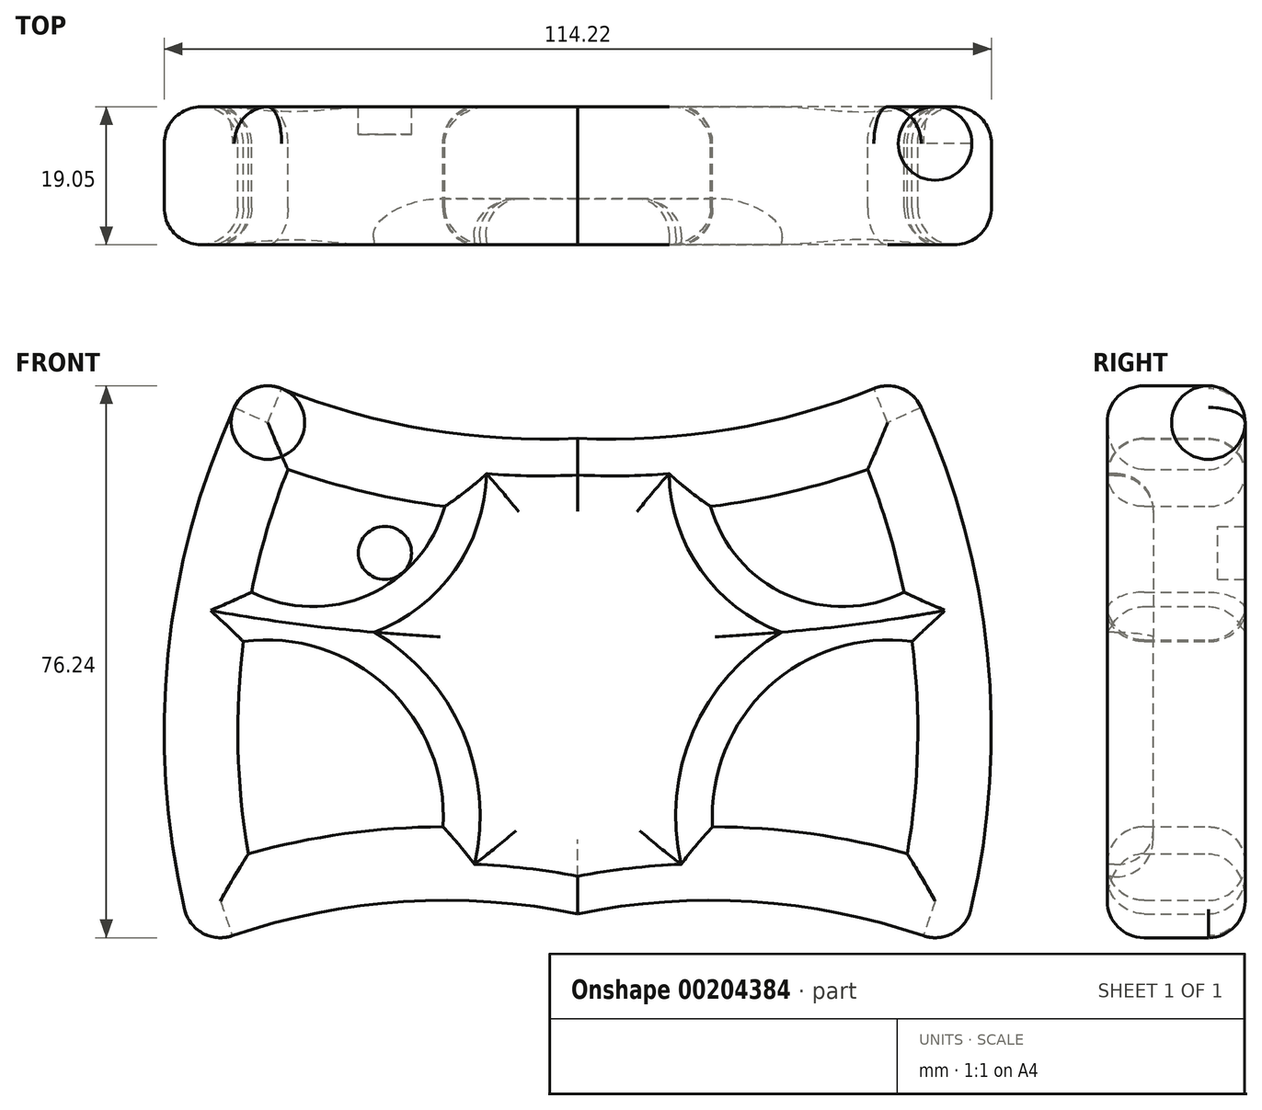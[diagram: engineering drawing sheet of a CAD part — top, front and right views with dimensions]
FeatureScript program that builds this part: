
annotation { "Feature Type Name" : "Feature", "Feature Type Description" : "" }
export const myFeature = defineFeature(function(context is Context, id is Id, definition is map)
    precondition{}
    {
        {
            var Q0;
            Q0=qCreatedBy(makeId("Front.planeOp"),FACE);
            var sketch = newSketch(context, id + "F0", { "sketchPlane" : qUnion([Q0])});
            skArc(sketch, "E0", {"start": v(0, 27) * mm, "mid": v(23.16, 28.63) * mm, "end": v(45.25, 35.77) * mm});
            skArc(sketch, "E1", {"start": v(52.85, -43.65) * mm, "mid": v(56.62, -3.22) * mm, "end": v(45.25, 35.77) * mm});
            skArc(sketch, "E2", {"start": v(52.85, -43.65) * mm, "mid": v(26.8, -37.23) * mm, "end": v(0, -38.69) * mm});
            skArc(sketch, "E3.0", {"start": v(43.09, -40.83) * mm, "mid": v(43.16, -40.57) * mm, "end": v(43.23, -40.32) * mm});
            skArc(sketch, "E4.0", {"start": v(0, 16.83) * mm, "mid": v(20.3, 17.85) * mm, "end": v(40.03, 22.7) * mm});
            skArc(sketch, "E5.0", {"start": v(56.7, -34.25) * mm, "mid": v(55.97, -33.95) * mm, "end": v(55.23, -33.66) * mm});
            skArc(sketch, "E6.trimOffspring", {"start": v(49.45, 26.51) * mm, "mid": v(49.48, 26.53) * mm, "end": v(49.52, 26.54) * mm});
            skArc(sketch, "E7.trimOffspring", {"start": v(45.5, -30.4) * mm, "mid": v(22.87, -26.77) * mm, "end": v(0, -28.34) * mm});
            skArc(sketch, "E8.trimOffspring", {"start": v(45.5, -30.4) * mm, "mid": v(46.44, -3.47) * mm, "end": v(40.03, 22.7) * mm});
            skPoint(sketch, "E9", {"position": v(0, -28.34) * mm});
            skPoint(sketch, "E10", {"position": v(0, 16.83) * mm});
            skArc(sketch, "E11", {"start": v(18.36, 17.58) * mm, "mid": v(28.9, 5.37) * mm, "end": v(45.04, 5.76) * mm});
            skArc(sketch, "E12", {"start": v(46.16, -1.09) * mm, "mid": v(26.35, -7.37) * mm, "end": v(18.62, -26.67) * mm});
            skPoint(sketch, "E13", {"position": v(23.95, 8.57) * mm});
            skPoint(sketch, "E14", {"position": v(28.28, 5.66) * mm});
            skArc(sketch, "E15.MirrorCS", {"start": v(0, 27) * mm, "mid": v(-23.16, 28.63) * mm, "end": v(-45.25, 35.77) * mm});
            skArc(sketch, "E16.MirrorCS", {"start": v(-52.85, -43.65) * mm, "mid": v(-56.62, -3.22) * mm, "end": v(-45.25, 35.77) * mm});
            skArc(sketch, "E17.MirrorCS", {"start": v(-49.45, 26.51) * mm, "mid": v(-49.48, 26.53) * mm, "end": v(-49.52, 26.54) * mm});
            skArc(sketch, "E18.MirrorCS", {"start": v(-56.7, -34.25) * mm, "mid": v(-55.97, -33.95) * mm, "end": v(-55.23, -33.66) * mm});
            skArc(sketch, "E19.MirrorCS", {"start": v(-43.09, -40.83) * mm, "mid": v(-43.16, -40.57) * mm, "end": v(-43.23, -40.32) * mm});
            skPoint(sketch, "E20.MirrorP", {"position": v(-28.28, 5.66) * mm});
            skArc(sketch, "E21.MirrorCS", {"start": v(-52.85, -43.65) * mm, "mid": v(-26.8, -37.23) * mm, "end": v(0, -38.69) * mm});
            skPoint(sketch, "E22.MirrorP", {"position": v(-23.95, 8.57) * mm});
            skArc(sketch, "E23.MirrorCS", {"start": v(-46.16, -1.09) * mm, "mid": v(-26.35, -7.37) * mm, "end": v(-18.62, -26.67) * mm});
            skArc(sketch, "E24.MirrorCS", {"start": v(-18.36, 17.58) * mm, "mid": v(-28.9, 5.37) * mm, "end": v(-45.04, 5.76) * mm});
            skArc(sketch, "E25.MirrorCS", {"start": v(-45.5, -30.4) * mm, "mid": v(-22.87, -26.77) * mm, "end": v(0, -28.34) * mm});
            skArc(sketch, "E26.MirrorCS", {"start": v(-45.5, -30.4) * mm, "mid": v(-46.44, -3.47) * mm, "end": v(-40.03, 22.7) * mm});
            skArc(sketch, "E27.MirrorCS", {"start": v(0, 16.83) * mm, "mid": v(-20.3, 17.85) * mm, "end": v(-40.03, 22.7) * mm});
            skCircle(sketch, "E28", {"center": v(-27.34, 9.91) * mm, "radius": 3.18 * mm});
            skLineSegment(sketch, "E29", {"start": v(-30.28, 8.71) * mm, "end": v(-28.9, 5.37) * mm});
            skLineSegment(sketch, "E30", {"start": v(-25.02, 12.08) * mm, "end": v(-22.8, 9.7) * mm});
            skSolve(sketch);
        }
        {
            var Q0;
            Q0 = qSketchRegion(id + "F0", true);
            var Q1;
            {var subQ0=sQuery(id+"F0.wireOp",EDGE,"E11");Q1=makeQuery(id+"F0.imprint","IMPRINT",FACE,{"disambiguationData":[TD([[makeQuery(id+"F0.imprint","IMPRINT",EDGE,{"derivedFrom":subQ0}),-1.0]])]});}
            extrude(context, id + "F1", {"entities" : qUnion([Q0, Q1]), "depth" : 19.05 * mm});
        }
        {
            var Q0;
            Q0=makeQuery(id+"F1.opExtrude","CAP_EDGE",EDGE,{"disambiguationData":[OSD([sQuery(id+"F0.wireOp",EDGE,"E16.MirrorCS")])],"isStart":false});
            fillet(context, id + "F2", {"entities" : qUnion([Q0]), "radius" : 5.08 * mm, "tangentPropagation" : true, "allowEdgeOverflow" : false});
        }
        {
            var Q0;
            Q0=makeQuery(id+"F1.opExtrude","CAP_FACE",FACE,{"disambiguationData":[OSD([sQuery(id+"F0.wireOp",EDGE,"E0"),sQuery(id+"F0.wireOp",EDGE,"E1"),sQuery(id+"F0.wireOp",EDGE,"E2"),sQuery(id+"F0.wireOp",EDGE,"E4.0"),sQuery(id+"F0.wireOp",EDGE,"E7.trimOffspring"),sQuery(id+"F0.wireOp",EDGE,"E8.trimOffspring"),sQuery(id+"F0.wireOp",EDGE,"E11"),sQuery(id+"F0.wireOp",EDGE,"E12"),sQuery(id+"F0.wireOp",EDGE,"E15.MirrorCS"),sQuery(id+"F0.wireOp",EDGE,"E16.MirrorCS"),sQuery(id+"F0.wireOp",EDGE,"E21.MirrorCS"),sQuery(id+"F0.wireOp",EDGE,"E23.MirrorCS"),sQuery(id+"F0.wireOp",EDGE,"E24.MirrorCS"),sQuery(id+"F0.wireOp",EDGE,"E25.MirrorCS"),sQuery(id+"F0.wireOp",EDGE,"E26.MirrorCS"),sQuery(id+"F0.wireOp",EDGE,"E27.MirrorCS")])],"isStart":true});
            fillet(context, id + "F3", {"entities" : qUnion([Q0]), "radius" : 5.08 * mm, "tangentPropagation" : true, "allowEdgeOverflow" : false});
        }
        {
            var Q0;
            Q0=makeQuery(id+"F1.opExtrude","CAP_EDGE",EDGE,{"disambiguationData":[OSD([sQuery(id+"F0.wireOp",EDGE,"E1")])],"isStart":false});
            fillet(context, id + "F4", {"entities" : qUnion([Q0]), "radius" : 5.08 * mm, "tangentPropagation" : true, "allowEdgeOverflow" : false});
        }
        {
            var Q0;
            Q0=makeQuery(id+"F1.opExtrude","CAP_FACE",FACE,{"disambiguationData":[OSD([sQuery(id+"F0.wireOp",EDGE,"E0"),sQuery(id+"F0.wireOp",EDGE,"E1"),sQuery(id+"F0.wireOp",EDGE,"E2"),sQuery(id+"F0.wireOp",EDGE,"E4.0"),sQuery(id+"F0.wireOp",EDGE,"E7.trimOffspring"),sQuery(id+"F0.wireOp",EDGE,"E8.trimOffspring"),sQuery(id+"F0.wireOp",EDGE,"E11"),sQuery(id+"F0.wireOp",EDGE,"E12"),sQuery(id+"F0.wireOp",EDGE,"E15.MirrorCS"),sQuery(id+"F0.wireOp",EDGE,"E16.MirrorCS"),sQuery(id+"F0.wireOp",EDGE,"E21.MirrorCS"),sQuery(id+"F0.wireOp",EDGE,"E23.MirrorCS"),sQuery(id+"F0.wireOp",EDGE,"E24.MirrorCS"),sQuery(id+"F0.wireOp",EDGE,"E25.MirrorCS"),sQuery(id+"F0.wireOp",EDGE,"E26.MirrorCS"),sQuery(id+"F0.wireOp",EDGE,"E27.MirrorCS")])],"isStart":false});
            fillet(context, id + "F5", {"entities" : qUnion([Q0]), "radius" : 5.08 * mm, "tangentPropagation" : true, "allowEdgeOverflow" : false});
        }
        {
            var Q0;
            Q0=makeQuery(id+"F5.opFillet","SPLIT",FACE,{"disambiguationData":[OD(2.0)],"derivedFrom":makeQuery(id+"F1.opExtrude","CAP_FACE",FACE,{"disambiguationData":[OSD([sQuery(id+"F0.wireOp",EDGE,"E0"),sQuery(id+"F0.wireOp",EDGE,"E1"),sQuery(id+"F0.wireOp",EDGE,"E2"),sQuery(id+"F0.wireOp",EDGE,"E4.0"),sQuery(id+"F0.wireOp",EDGE,"E7.trimOffspring"),sQuery(id+"F0.wireOp",EDGE,"E8.trimOffspring"),sQuery(id+"F0.wireOp",EDGE,"E11"),sQuery(id+"F0.wireOp",EDGE,"E12"),sQuery(id+"F0.wireOp",EDGE,"E15.MirrorCS"),sQuery(id+"F0.wireOp",EDGE,"E16.MirrorCS"),sQuery(id+"F0.wireOp",EDGE,"E21.MirrorCS"),sQuery(id+"F0.wireOp",EDGE,"E23.MirrorCS"),sQuery(id+"F0.wireOp",EDGE,"E24.MirrorCS"),sQuery(id+"F0.wireOp",EDGE,"E25.MirrorCS"),sQuery(id+"F0.wireOp",EDGE,"E26.MirrorCS"),sQuery(id+"F0.wireOp",EDGE,"E27.MirrorCS")])],"isStart":false})});
            extrude(context, id + "F6", {"entities" : qUnion([Q0]), "operationType" : NewBodyOperationType.REMOVE, "oppositeDirection" : true, "depth" : 6.35 * mm, "hasDraft" : true, "draftAngle" : 3 * degree});
        }
        {
            var Q0;
            Q0=makeQuery(id+"F6.boolean.opBoolean","COPY",FACE,{"derivedFrom":makeQuery(id+"F6.opExtrude","CAP_FACE",FACE,{"disambiguationData":[OSD([sQuery(id+"F0.wireOp",EDGE,"E0"),sQuery(id+"F0.wireOp",EDGE,"E1"),sQuery(id+"F0.wireOp",EDGE,"E2"),sQuery(id+"F0.wireOp",EDGE,"E4.0"),sQuery(id+"F0.wireOp",EDGE,"E7.trimOffspring"),sQuery(id+"F0.wireOp",EDGE,"E8.trimOffspring"),sQuery(id+"F0.wireOp",EDGE,"E11"),sQuery(id+"F0.wireOp",EDGE,"E12"),sQuery(id+"F0.wireOp",EDGE,"E15.MirrorCS"),sQuery(id+"F0.wireOp",EDGE,"E16.MirrorCS"),sQuery(id+"F0.wireOp",EDGE,"E21.MirrorCS"),sQuery(id+"F0.wireOp",EDGE,"E23.MirrorCS"),sQuery(id+"F0.wireOp",EDGE,"E24.MirrorCS"),sQuery(id+"F0.wireOp",EDGE,"E25.MirrorCS"),sQuery(id+"F0.wireOp",EDGE,"E26.MirrorCS"),sQuery(id+"F0.wireOp",EDGE,"E27.MirrorCS")])],"isStart":false})});
            fillet(context, id + "F7", {"entities" : qUnion([Q0]), "radius" : 5.08 * mm, "tangentPropagation" : true, "allowEdgeOverflow" : false});
        }
        {
            var Q0;
            Q0=qCreatedBy(makeId("Front.planeOp"),FACE);
            var sketch = newSketch(context, id + "F8", { "sketchPlane" : qUnion([Q0])});
            skCircle(sketch, "E31", {"center": v(-26.62, 11.17) * mm, "radius": 3.67 * mm});
            skLineSegment(sketch, "E32", {"start": v(-29.76, 9.26) * mm, "end": v(-29.2, 5.4) * mm});
            skLineSegment(sketch, "E33", {"start": v(-24.9, 14.41) * mm, "end": v(-20.98, 12.34) * mm});
            skSolve(sketch);
        }
        {
            var Q0;
            {var subQ0=sQuery(id+"F8.wireOp",EDGE,"E31");var subQ1=makeQuery(id+"F8.imprint","IMPRINT",VERTEX,{"disambiguationData":[OD(0.0)],"derivedFrom":subQ0});Q0=makeQuery(id+"F8.imprint","IMPRINT",FACE,{"disambiguationData":[TD([[makeQuery(id+"F8.imprint","IMPRINT",EDGE,{"disambiguationData":[TD([[subQ1,1.0]])],"derivedFrom":subQ0}),1.0]])]});}
            var Q1;
            Q1=sQuery(id+"F0.wireOp",EDGE,"E28");
            var Q2;
            Q2=sQuery(id+"F0.wireOp",EDGE,"E30");
            var Q3;
            Q3=sQuery(id+"F0.wireOp",EDGE,"E29");
            extrude(context, id + "F9", {"entities" : qUnion([Q0]), "surfaceEntities" : qUnion([Q1, Q2, Q3]), "depth" : 3.8 * mm});
        }
    });
